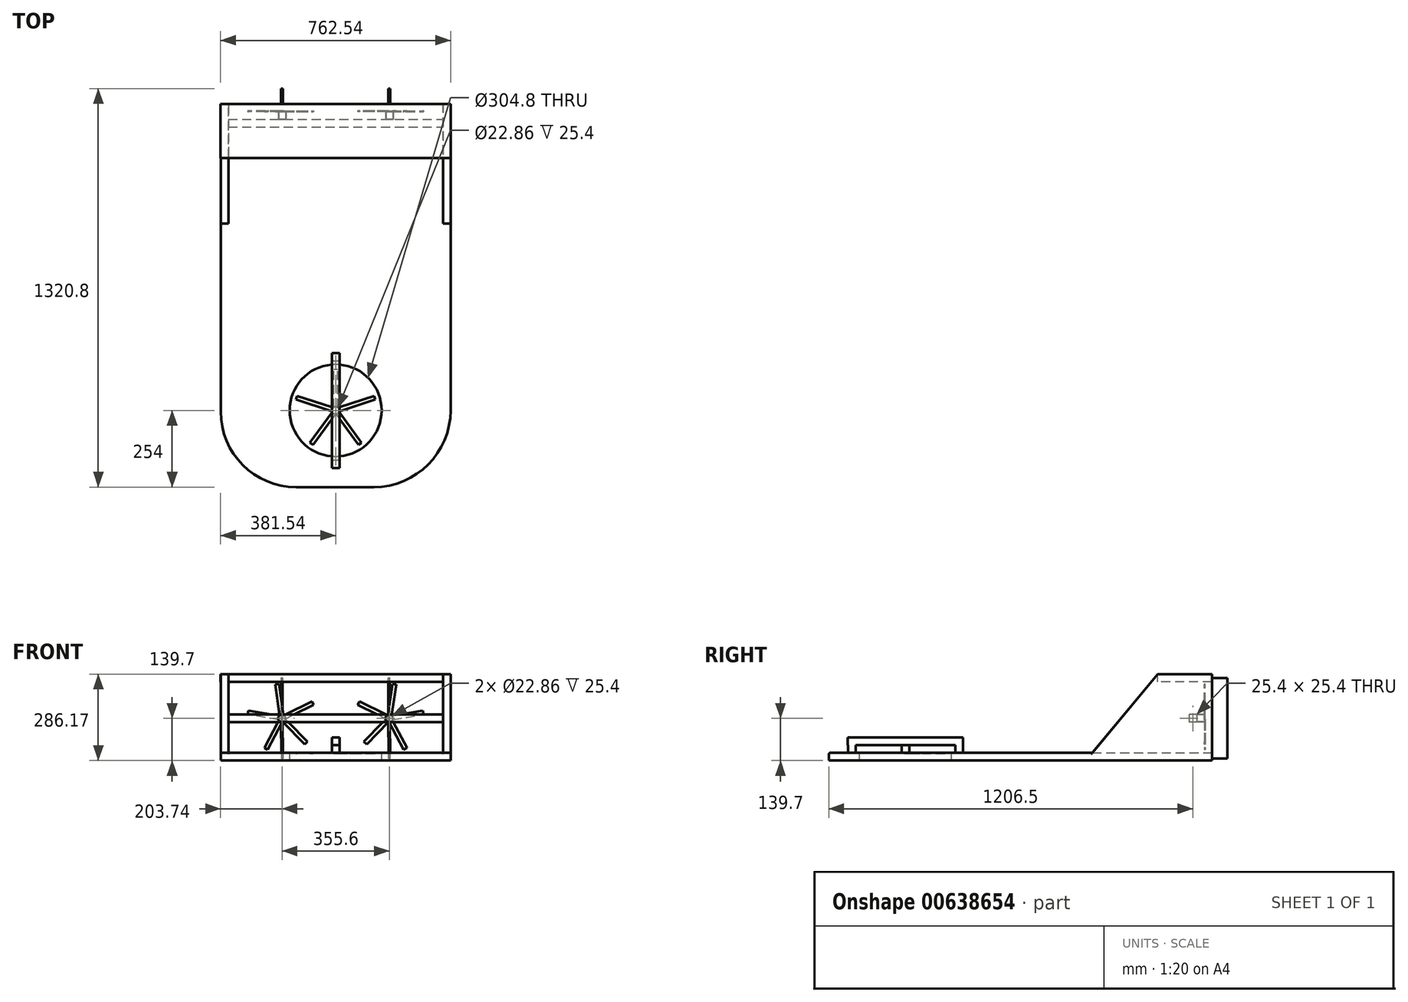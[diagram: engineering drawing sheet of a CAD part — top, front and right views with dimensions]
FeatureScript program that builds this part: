
annotation { "Feature Type Name" : "Feature", "Feature Type Description" : "" }
export const myFeature = defineFeature(function(context is Context, id is Id, definition is map)
    precondition{}
    {
        {
            var Q0;
            Q0=qCreatedBy(makeId("Top.planeOp"),FACE);
            var sketch = newSketch(context, id + "F0", { "sketchPlane" : qUnion([Q0])});
            skLineSegment(sketch, "E0.bottom", {"start": v(-381, 635) * mm, "end": v(381, 635) * mm});
            skLineSegment(sketch, "E0.top", {"start": v(-131, -635) * mm, "end": v(127, -635) * mm});
            skLineSegment(sketch, "E0.left", {"start": v(-381, 635) * mm, "end": v(-381, -385) * mm});
            skLineSegment(sketch, "E0.right", {"start": v(381, 635) * mm, "end": v(381, -381) * mm});
            skPoint(sketch, "E0.middle", {"position": v(0, 0) * mm});
            skPoint(sketch, "E1.visualSharp", {"position": v(-381, -635) * mm});
            skArc(sketch, "E1.filletArc", {"start": v(-381, -385) * mm, "mid": v(-307.78, -561.78) * mm, "end": v(-131, -635) * mm});
            skPoint(sketch, "E2.visualSharp", {"position": v(381, -635) * mm});
            skArc(sketch, "E2.filletArc", {"start": v(127, -635) * mm, "mid": v(306.6, -560.6) * mm, "end": v(381, -381) * mm});
            skPoint(sketch, "E3", {"position": v(0, -381) * mm});
            skCircle(sketch, "E4", {"center": v(0, -381) * mm, "radius": 152.4 * mm});
            skSolve(sketch);
        }
        {
            var Q0;
            Q0 = qSketchRegion(id + "F0", true);
            extrude(context, id + "F1", {"entities" : qUnion([Q0]), "oppositeDirection" : true, "depth" : 25.4 * mm, "offsetDistance" : 25.4 * mm});
        }
        {
            var Q0;
            Q0=makeQuery(id+"F1.opExtrude","CAP_EDGE",EDGE,{"disambiguationData":[OSD([sQuery(id+"F0.wireOp",EDGE,"E0.left")])],"isStart":true});
            var Q1;
            Q1=makeQuery(id+"F1.opExtrude","CAP_EDGE",EDGE,{"disambiguationData":[OSD([sQuery(id+"F0.wireOp",EDGE,"E1.filletArc")])],"isStart":true});
            var Q2;
            Q2=makeQuery(id+"F1.opExtrude","CAP_EDGE",EDGE,{"disambiguationData":[OSD([sQuery(id+"F0.wireOp",EDGE,"E0.top")])],"isStart":true});
            var Q3;
            Q3=makeQuery(id+"F1.opExtrude","CAP_EDGE",EDGE,{"disambiguationData":[OSD([sQuery(id+"F0.wireOp",EDGE,"E2.filletArc")])],"isStart":true});
            var Q4;
            Q4=makeQuery(id+"F1.opExtrude","CAP_EDGE",EDGE,{"disambiguationData":[OSD([sQuery(id+"F0.wireOp",EDGE,"E0.right")])],"isStart":true});
            var Q5;
            Q5=makeQuery(id+"F1.opExtrude","CAP_EDGE",EDGE,{"disambiguationData":[OSD([sQuery(id+"F0.wireOp",EDGE,"E0.bottom")])],"isStart":true});
            fillet(context, id + "F2", {"entities" : qUnion([Q0, Q1, Q2, Q3, Q4, Q5]), "radius" : 5.08 * mm, "tangentPropagation" : true, "allowEdgeOverflow" : false});
        }
        {
            var Q0;
            Q0=makeQuery(id+"F1.opExtrude","CAP_FACE",FACE,{"disambiguationData":[OSD([sQuery(id+"F0.wireOp",EDGE,"E0.bottom"),sQuery(id+"F0.wireOp",EDGE,"E0.top"),sQuery(id+"F0.wireOp",EDGE,"E0.left"),sQuery(id+"F0.wireOp",EDGE,"E0.right"),sQuery(id+"F0.wireOp",EDGE,"E1.filletArc"),sQuery(id+"F0.wireOp",EDGE,"E2.filletArc"),sQuery(id+"F0.wireOp",EDGE,"E4")])],"isStart":true});
            var sketch = newSketch(context, id + "F3", { "sketchPlane" : qUnion([Q0])});
            skLineSegment(sketch, "E5.bottom", {"start": v(-12.7, -215.9) * mm, "end": v(12.7, -215.9) * mm});
            skLineSegment(sketch, "E5.top", {"start": v(-12.7, -190.5) * mm, "end": v(12.7, -190.5) * mm});
            skLineSegment(sketch, "E5.left", {"start": v(-12.7, -215.9) * mm, "end": v(-12.7, -190.5) * mm});
            skLineSegment(sketch, "E5.right", {"start": v(12.7, -215.9) * mm, "end": v(12.7, -190.5) * mm});
            skPoint(sketch, "E5.middle", {"position": v(0, -203.2) * mm});
            skLineSegment(sketch, "E6.bottom", {"start": v(-12.7, -545.89) * mm, "end": v(12.7, -545.89) * mm});
            skLineSegment(sketch, "E6.top", {"start": v(-12.7, -571.71) * mm, "end": v(12.7, -571.71) * mm});
            skLineSegment(sketch, "E6.left", {"start": v(-12.7, -545.89) * mm, "end": v(-12.7, -571.71) * mm});
            skLineSegment(sketch, "E6.right", {"start": v(12.7, -545.89) * mm, "end": v(12.7, -571.71) * mm});
            skPoint(sketch, "E6.middle", {"position": v(0, -558.8) * mm});
            skSolve(sketch);
        }
        {
            var Q0;
            Q0 = qSketchRegion(id + "F3", true);
            extrude(context, id + "F4", {"entities" : qUnion([Q0]), "operationType" : NewBodyOperationType.ADD, "depth" : 25.4 * mm, "offsetDistance" : 25.4 * mm});
        }
        {
            var Q0;
            Q0=makeQuery(id+"F4.opExtrude","CAP_FACE",FACE,{"disambiguationData":[OSD([sQuery(id+"F3.wireOp",EDGE,"E5.bottom"),sQuery(id+"F3.wireOp",EDGE,"E5.top"),sQuery(id+"F3.wireOp",EDGE,"E5.left"),sQuery(id+"F3.wireOp",EDGE,"E5.right")])],"isStart":false});
            var sketch = newSketch(context, id + "F5", { "sketchPlane" : qUnion([Q0])});
            skLineSegment(sketch, "E7.bottom", {"start": v(-12.7, -190.5) * mm, "end": v(12.7, -190.5) * mm});
            skLineSegment(sketch, "E7.top", {"start": v(-12.7, -571.85) * mm, "end": v(12.7, -571.85) * mm});
            skLineSegment(sketch, "E7.left", {"start": v(-12.7, -190.5) * mm, "end": v(-12.7, -571.85) * mm});
            skLineSegment(sketch, "E7.right", {"start": v(12.7, -190.5) * mm, "end": v(12.7, -571.85) * mm});
            skSolve(sketch);
        }
        {
            var Q0;
            Q0 = qSketchRegion(id + "F5", true);
            extrude(context, id + "F6", {"entities" : qUnion([Q0]), "operationType" : NewBodyOperationType.ADD, "depth" : 25.4 * mm, "offsetDistance" : 25.4 * mm});
        }
        {
            var Q0;
            Q0=makeQuery(id+"F1.opExtrude","SWEPT_FACE",FACE,{"disambiguationData":[OSD([sQuery(id+"F0.wireOp",EDGE,"E0.right")])]});
            var sketch = newSketch(context, id + "F7", { "sketchPlane" : qUnion([Q0])});
            skLineSegment(sketch, "E8", {"start": v(635, -5.08) * mm, "end": v(635, 260.77) * mm});
            skLineSegment(sketch, "E9", {"start": v(635, 260.77) * mm, "end": v(455.73, 260.77) * mm});
            skLineSegment(sketch, "E10", {"start": v(455.73, 260.77) * mm, "end": v(234.4, -5.08) * mm});
            skLineSegment(sketch, "E11", {"start": v(234.4, -5.08) * mm, "end": v(635, -5.08) * mm});
            skSolve(sketch);
        }
        {
            var Q0;
            Q0 = qSketchRegion(id + "F7", true);
            extrude(context, id + "F8", {"entities" : qUnion([Q0]), "oppositeDirection" : true, "depth" : 25.4 * mm, "offsetDistance" : 25.4 * mm});
        }
        {
            var Q0;
            Q0=makeQuery(id+"F8.opExtrude","SWEPT_BODY",BODY,{"disambiguationData":[OSD([sQuery(id+"F7.wireOp",EDGE,"E8"),sQuery(id+"F7.wireOp",EDGE,"E9"),sQuery(id+"F7.wireOp",EDGE,"E10"),sQuery(id+"F7.wireOp",EDGE,"E11")])]});
            var Q1;
            Q1=qCreatedBy(makeId("Right.planeOp"),FACE);
            mirror(context, id + "F9", {"operationType" : NewBodyOperationType.ADD, "entities" : qUnion([Q0]), "mirrorPlane" : qUnion([Q1])});
        }
        {
            var Q0;
            Q0=makeQuery(id+"F8.opExtrude","SWEPT_FACE",FACE,{"disambiguationData":[OSD([sQuery(id+"F7.wireOp",EDGE,"E9")])]});
            var sketch = newSketch(context, id + "F10", { "sketchPlane" : qUnion([Q0])});
            skLineSegment(sketch, "E12.bottom", {"start": v(381, 635) * mm, "end": v(-381.54, 635) * mm});
            skLineSegment(sketch, "E12.top", {"start": v(381, 455.3) * mm, "end": v(-381.54, 455.3) * mm});
            skLineSegment(sketch, "E12.left", {"start": v(381, 635) * mm, "end": v(381, 455.3) * mm});
            skLineSegment(sketch, "E12.right", {"start": v(-381.54, 635) * mm, "end": v(-381.54, 455.3) * mm});
            skSolve(sketch);
        }
        {
            var Q0;
            {var subQ3=sQuery(id+"F10.wireOp",EDGE,"E12.top");Q0=makeQuery(id+"F10.imprint","IMPRINT",FACE,{"disambiguationData":[TD([[makeQuery(id+"F10.imprint","IMPRINT",EDGE,{"derivedFrom":subQ3}),-1.0]])]});}
            extrude(context, id + "F11", {"entities" : qUnion([Q0]), "operationType" : NewBodyOperationType.ADD, "oppositeDirection" : true, "depth" : 25.4 * mm, "offsetDistance" : 25.4 * mm});
        }
        {
            var Q0;
            Q0=makeQuery(id+"F8.opExtrude","CAP_FACE",FACE,{"disambiguationData":[OSD([sQuery(id+"F7.wireOp",EDGE,"E8"),sQuery(id+"F7.wireOp",EDGE,"E9"),sQuery(id+"F7.wireOp",EDGE,"E10"),sQuery(id+"F7.wireOp",EDGE,"E11")])],"isStart":false});
            var sketch = newSketch(context, id + "F12", { "sketchPlane" : qUnion([Q0])});
            skPoint(sketch, "E13", {"position": v(-571.5, 114.3) * mm});
            skLineSegment(sketch, "E14.bottom", {"start": v(-584.2, 127) * mm, "end": v(-558.8, 127) * mm});
            skLineSegment(sketch, "E14.top", {"start": v(-584.2, 101.6) * mm, "end": v(-558.8, 101.6) * mm});
            skLineSegment(sketch, "E14.left", {"start": v(-584.2, 127) * mm, "end": v(-584.2, 101.6) * mm});
            skLineSegment(sketch, "E14.right", {"start": v(-558.8, 127) * mm, "end": v(-558.8, 101.6) * mm});
            skSolve(sketch);
        }
        {
            var Q0;
            Q0 = qSketchRegion(id + "F12", true);
            extrude(context, id + "F13", {"entities" : qUnion([Q0]), "operationType" : NewBodyOperationType.ADD, "endBound" : BoundingType.UP_TO_NEXT, "depth" : 25.4 * mm, "offsetDistance" : 25.4 * mm});
        }
        {
            var Q0;
            Q0=makeQuery(id+"F13.opExtrude","SWEPT_FACE",FACE,{"disambiguationData":[OSD([sQuery(id+"F12.wireOp",EDGE,"E14.left")])]});
            var sketch = newSketch(context, id + "F14", { "sketchPlane" : qUnion([Q0])});
            skPoint(sketch, "E15", {"position": v(-177.8, 114.3) * mm});
            skPoint(sketch, "E16", {"position": v(177.8, 114.3) * mm});
            skPoint(sketch, "E17", {"position": v(-355.6, 114.3) * mm});
            skPoint(sketch, "E18", {"position": v(355.6, 114.3) * mm});
            skCircle(sketch, "E19", {"center": v(-177.8, 114.3) * mm, "radius": 12.7 * mm});
            skCircle(sketch, "E20", {"center": v(177.8, 114.3) * mm, "radius": 12.7 * mm});
            skCircle(sketch, "E21", {"center": v(-177.8, 114.3) * mm, "radius": 11.43 * mm});
            skCircle(sketch, "E22", {"center": v(177.8, 114.3) * mm, "radius": 11.43 * mm});
            skSolve(sketch);
        }
        {
            var Q0;
            Q0 = qSketchRegion(id + "F14", true);
            var Q1;
            Q1 = qConstructionFilter(qBodyType(qCreatedBy(id + "F14" ,EDGE), BodyType.WIRE), ConstructionObject.NO);
            extrude(context, id + "F15", {"entities" : qUnion([Q0]), "surfaceEntities" : qUnion([Q1]), "depth" : 25.4 * mm, "offsetDistance" : 25.4 * mm});
        }
        {
            var Q0;
            Q0=makeQuery(id+"F15.opExtrude","CAP_FACE",FACE,{"disambiguationData":[OSD([sQuery(id+"F14.wireOp",EDGE,"E19"),sQuery(id+"F14.wireOp",EDGE,"E21")])],"isStart":false});
            var sketch = newSketch(context, id + "F16", { "sketchPlane" : qUnion([Q0])});
            skPoint(sketch, "E23.0.midPoint", {"position": v(-135.12, 195.8) * mm});
            skLineSegment(sketch, "E24.0", {"start": v(-174.98, 108.61) * mm, "end": v(-73.09, 159.1) * mm});
            skLineSegment(sketch, "E25.0", {"start": v(-180.62, 119.99) * mm, "end": v(-78.73, 170.49) * mm});
            skLineSegment(sketch, "E26.0", {"start": v(-171.52, 115.22) * mm, "end": v(-188.06, 227.73) * mm});
            skLineSegment(sketch, "E27.0", {"start": v(-184.08, 113.38) * mm, "end": v(-200.62, 225.89) * mm});
            skLineSegment(sketch, "E28.0", {"start": v(-176.74, 120.56) * mm, "end": v(-288.85, 139.6) * mm});
            skLineSegment(sketch, "E29.0", {"start": v(-178.86, 108.04) * mm, "end": v(-290.98, 127.08) * mm});
            skLineSegment(sketch, "E30.0", {"start": v(-183.43, 117.25) * mm, "end": v(-236.18, 16.5) * mm});
            skLineSegment(sketch, "E31.0", {"start": v(-172.17, 111.35) * mm, "end": v(-224.92, 10.61) * mm});
            skLineSegment(sketch, "E32.0", {"start": v(-182.34, 109.86) * mm, "end": v(-102.83, 28.56) * mm});
            skLineSegment(sketch, "E33.0", {"start": v(-173.26, 118.74) * mm, "end": v(-93.75, 37.44) * mm});
            skLineSegment(sketch, "E34", {"start": v(-78.73, 170.49) * mm, "end": v(-73.09, 159.1) * mm});
            skLineSegment(sketch, "E35", {"start": v(-200.62, 225.89) * mm, "end": v(-188.06, 227.73) * mm});
            skLineSegment(sketch, "E36", {"start": v(-290.98, 127.08) * mm, "end": v(-288.85, 139.6) * mm});
            skLineSegment(sketch, "E37", {"start": v(-236.18, 16.5) * mm, "end": v(-224.92, 10.61) * mm});
            skLineSegment(sketch, "E38", {"start": v(-102.83, 28.56) * mm, "end": v(-93.75, 37.44) * mm});
            skLineSegment(sketch, "E39.MirrorCS", {"start": v(176.74, 120.56) * mm, "end": v(288.85, 139.6) * mm});
            skLineSegment(sketch, "E40.MirrorCS", {"start": v(178.86, 108.04) * mm, "end": v(290.98, 127.08) * mm});
            skLineSegment(sketch, "E41.MirrorCS", {"start": v(290.98, 127.08) * mm, "end": v(288.85, 139.6) * mm});
            skLineSegment(sketch, "E42.MirrorCS", {"start": v(183.43, 117.25) * mm, "end": v(236.18, 16.5) * mm});
            skLineSegment(sketch, "E43.MirrorCS", {"start": v(236.18, 16.5) * mm, "end": v(224.92, 10.61) * mm});
            skLineSegment(sketch, "E44.MirrorCS", {"start": v(172.17, 111.35) * mm, "end": v(224.92, 10.61) * mm});
            skLineSegment(sketch, "E45.MirrorCS", {"start": v(182.34, 109.86) * mm, "end": v(102.83, 28.56) * mm});
            skLineSegment(sketch, "E46.MirrorCS", {"start": v(173.26, 118.74) * mm, "end": v(93.75, 37.44) * mm});
            skLineSegment(sketch, "E47.MirrorCS", {"start": v(102.83, 28.56) * mm, "end": v(93.75, 37.44) * mm});
            skLineSegment(sketch, "E48.MirrorCS", {"start": v(174.98, 108.61) * mm, "end": v(73.09, 159.1) * mm});
            skLineSegment(sketch, "E49.MirrorCS", {"start": v(180.62, 119.99) * mm, "end": v(78.73, 170.49) * mm});
            skLineSegment(sketch, "E50.MirrorCS", {"start": v(78.73, 170.49) * mm, "end": v(73.09, 159.1) * mm});
            skLineSegment(sketch, "E51.MirrorCS", {"start": v(171.52, 115.22) * mm, "end": v(188.06, 227.73) * mm});
            skLineSegment(sketch, "E52.MirrorCS", {"start": v(184.08, 113.38) * mm, "end": v(200.62, 225.89) * mm});
            skLineSegment(sketch, "E53.MirrorCS", {"start": v(200.62, 225.89) * mm, "end": v(188.06, 227.73) * mm});
            skSolve(sketch);
        }
        {
            var Q0;
            Q0 = qSketchRegion(id + "F16", true);
            extrude(context, id + "F17", {"entities" : qUnion([Q0]), "depth" : 2.54 * mm, "offsetDistance" : 25.4 * mm});
        }
        {
            var Q0;
            {var subQ0=makeQuery(id+"F8.opExtrude","SWEPT_FACE",FACE,{"disambiguationData":[OSD([sQuery(id+"F7.wireOp",EDGE,"E8")])]});Q0=makeQuery(id+"F11.boolean.opBoolean","MERGE",FACE,{"derivedFrom":[makeQuery(id+"F9.boolean.opBoolean","MERGE",FACE,{"derivedFrom":[makeQuery(id+"F1.opExtrude","SWEPT_FACE",FACE,{"disambiguationData":[OSD([sQuery(id+"F0.wireOp",EDGE,"E0.bottom")])]}),subQ0,makeQuery(id+"F9.opPattern","COPY",FACE,{"derivedFrom":subQ0,"instanceName":"1"})]}),makeQuery(id+"F11.opExtrude","SWEPT_FACE",FACE,{"disambiguationData":[OSD([sQuery(id+"F10.wireOp",EDGE,"E12.bottom")])]})]});}
            var sketch = newSketch(context, id + "F18", { "sketchPlane" : qUnion([Q0])});
            skPoint(sketch, "E54", {"position": v(-177.26, 248.07) * mm});
            skPoint(sketch, "E55", {"position": v(-177.8, -18.63) * mm});
            skPoint(sketch, "E56", {"position": v(177.8, -18.63) * mm});
            skPoint(sketch, "E57", {"position": v(178.34, 248.07) * mm});
            skLineSegment(sketch, "E58.0", {"start": v(-175.26, -18.64) * mm, "end": v(-174.72, 248.06) * mm});
            skLineSegment(sketch, "E59.0", {"start": v(-180.34, -18.63) * mm, "end": v(-179.8, 248.07) * mm});
            skLineSegment(sketch, "E60", {"start": v(-179.8, 248.07) * mm, "end": v(-174.72, 248.06) * mm});
            skLineSegment(sketch, "E61", {"start": v(-180.34, -18.63) * mm, "end": v(-175.26, -18.64) * mm});
            skLineSegment(sketch, "E62.0", {"start": v(175.8, 248.07) * mm, "end": v(175.26, -18.63) * mm});
            skLineSegment(sketch, "E63.0", {"start": v(180.88, 248.06) * mm, "end": v(180.34, -18.64) * mm});
            skLineSegment(sketch, "E64", {"start": v(175.8, 248.07) * mm, "end": v(180.88, 248.06) * mm});
            skLineSegment(sketch, "E65", {"start": v(175.26, -18.63) * mm, "end": v(180.34, -18.64) * mm});
            skSolve(sketch);
        }
        {
            var Q0;
            Q0 = qSketchRegion(id + "F18", true);
            extrude(context, id + "F19", {"entities" : qUnion([Q0]), "operationType" : NewBodyOperationType.ADD, "depth" : 50.8 * mm, "offsetDistance" : 25.4 * mm});
        }
        {
            var Q0;
            {var subQ0=sQuery(id+"F5.wireOp",EDGE,"E7.right");var subQ1=sQuery(id+"F5.wireOp",EDGE,"E7.left");Q0=makeQuery(id+"F6.boolean.opBoolean","SPLIT",FACE,{"disambiguationData":[TD([makeQuery(id+"F4.opExtrude","SWEPT_FACE",FACE,{"disambiguationData":[OSD([sQuery(id+"F3.wireOp",EDGE,"E5.bottom")])]})])],"derivedFrom":makeQuery(id+"F6.opExtrude","CAP_FACE",FACE,{"disambiguationData":[OSD([sQuery(id+"F5.wireOp",EDGE,"E7.bottom"),sQuery(id+"F5.wireOp",EDGE,"E7.top"),subQ1,subQ0])],"isStart":true})});}
            var sketch = newSketch(context, id + "F20", { "sketchPlane" : qUnion([Q0])});
            skPoint(sketch, "E66", {"position": v(0, 381) * mm});
            skCircle(sketch, "E67", {"center": v(0, 381) * mm, "radius": 12.7 * mm});
            skCircle(sketch, "E68", {"center": v(0, 381) * mm, "radius": 11.43 * mm});
            skSolve(sketch);
        }
        {
            var Q0;
            Q0 = qSketchRegion(id + "F20", true);
            extrude(context, id + "F21", {"entities" : qUnion([Q0]), "operationType" : NewBodyOperationType.ADD, "depth" : 25.4 * mm, "offsetDistance" : 25.4 * mm});
        }
        {
            var Q0;
            Q0=makeQuery(id+"F21.opExtrude","CAP_FACE",FACE,{"disambiguationData":[OSD([sQuery(id+"F20.wireOp",EDGE,"E67"),sQuery(id+"F20.wireOp",EDGE,"E68")])],"isStart":false});
            var sketch = newSketch(context, id + "F22", { "sketchPlane" : qUnion([Q0])});
            skPoint(sketch, "E69.0.midPoint", {"position": v(0, 491.28) * mm});
            skLineSegment(sketch, "E70.0", {"start": v(1.96, 374.96) * mm, "end": v(-127.68, 332.84) * mm});
            skLineSegment(sketch, "E71.0", {"start": v(-1.96, 387.04) * mm, "end": v(-131.6, 344.91) * mm});
            skLineSegment(sketch, "E72.0", {"start": v(5.14, 384.73) * mm, "end": v(-74.99, 495.02) * mm});
            skLineSegment(sketch, "E73.0", {"start": v(-5.14, 377.27) * mm, "end": v(-85.26, 487.55) * mm});
            skLineSegment(sketch, "E74.0", {"start": v(5.14, 377.27) * mm, "end": v(85.26, 487.55) * mm});
            skLineSegment(sketch, "E75.0", {"start": v(-5.14, 384.73) * mm, "end": v(74.99, 495.02) * mm});
            skLineSegment(sketch, "E76.0", {"start": v(-1.96, 374.96) * mm, "end": v(127.68, 332.84) * mm});
            skLineSegment(sketch, "E77.0", {"start": v(1.96, 387.04) * mm, "end": v(131.6, 344.91) * mm});
            skLineSegment(sketch, "E78.0", {"start": v(-6.35, 381) * mm, "end": v(-6.35, 244.68) * mm});
            skLineSegment(sketch, "E79.0", {"start": v(6.35, 381) * mm, "end": v(6.35, 244.68) * mm});
            skLineSegment(sketch, "E80", {"start": v(-85.26, 487.55) * mm, "end": v(-74.99, 495.02) * mm});
            skLineSegment(sketch, "E81", {"start": v(-131.6, 344.91) * mm, "end": v(-127.68, 332.84) * mm});
            skLineSegment(sketch, "E82", {"start": v(-6.35, 244.68) * mm, "end": v(6.35, 244.68) * mm});
            skLineSegment(sketch, "E83", {"start": v(127.68, 332.84) * mm, "end": v(131.6, 344.91) * mm});
            skLineSegment(sketch, "E84", {"start": v(85.26, 487.55) * mm, "end": v(74.99, 495.02) * mm});
            skSolve(sketch);
        }
        {
            var Q0;
            Q0 = qSketchRegion(id + "F22", true);
            extrude(context, id + "F23", {"entities" : qUnion([Q0]), "depth" : 2.54 * mm, "offsetDistance" : 25.4 * mm});
        }
        {
            var Q0;
            {var subQ0=makeQuery(id+"F8.opExtrude","SWEPT_FACE",FACE,{"disambiguationData":[OSD([sQuery(id+"F7.wireOp",EDGE,"E8")])]});Q0=makeQuery(id+"F11.boolean.opBoolean","MERGE",FACE,{"derivedFrom":[makeQuery(id+"F9.boolean.opBoolean","MERGE",FACE,{"derivedFrom":[makeQuery(id+"F1.opExtrude","SWEPT_FACE",FACE,{"disambiguationData":[OSD([sQuery(id+"F0.wireOp",EDGE,"E0.bottom")])]}),subQ0,makeQuery(id+"F9.opPattern","COPY",FACE,{"derivedFrom":subQ0,"instanceName":"1"})]}),makeQuery(id+"F11.opExtrude","SWEPT_FACE",FACE,{"disambiguationData":[OSD([sQuery(id+"F10.wireOp",EDGE,"E12.bottom")])]})]});}
            var sketch = newSketch(context, id + "F24", { "sketchPlane" : qUnion([Q0])});
            skArc(sketch, "E85", {"start": v(-381, 12.7) * mm, "mid": v(-419.1, -25.55) * mm, "end": v(-380.7, -63.5) * mm});
            skLineSegment(sketch, "E86", {"start": v(-380.7, -63.5) * mm, "end": v(380.24, -63.5) * mm});
            skArc(sketch, "E87", {"start": v(380.24, -63.5) * mm, "mid": v(418.34, -25.78) * mm, "end": v(381, 12.7) * mm});
            skLineSegment(sketch, "E88", {"start": v(-381, 12.7) * mm, "end": v(-381, -25.4) * mm});
            skLineSegment(sketch, "E89", {"start": v(381, -25.4) * mm, "end": v(381, 12.7) * mm});
            skLineSegment(sketch, "E90", {"start": v(381, -25.4) * mm, "end": v(-381, -25.4) * mm});
            skSolve(sketch);
        }
        {
            var Q0;
            Q0=makeQuery(id+"F24.imprint","IMPRINT",FACE,{"disambiguationData":[TD([[makeQuery(id+"F24.imprint","IMPRINT",EDGE,{"derivedFrom":sQuery(id+"F24.wireOp",EDGE,"E85")}),1.0]])]});
            var Q1;
            Q1=sQuery(id+"F24.wireOp",EDGE,"E85");
            var Q2;
            Q2=sQuery(id+"F24.wireOp",EDGE,"E88");
            var Q3;
            Q3=sQuery(id+"F24.wireOp",EDGE,"E86");
            var Q4;
            Q4=sQuery(id+"F24.wireOp",EDGE,"E87");
            var Q5;
            Q5=sQuery(id+"F24.wireOp",EDGE,"E89");
            extrude(context, id + "F25", {"entities" : qUnion([Q0]), "bodyType" : ToolBodyType.SURFACE, "surfaceEntities" : qUnion([Q1, Q2, Q3, Q4, Q5]), "oppositeDirection" : true, "depth" : 1016 * mm, "offsetDistance" : 25.4 * mm, "hasSecondDirection" : true, "secondDirectionOppositeDirection" : false, "secondDirectionDepth" : 25.4 * mm});
        }
        {
            var Q0;
            Q0 = qSketchRegion(id + "F24", true);
            var Q1;
            Q1=makeQuery(id+"F25.opExtrude","CAP_EDGE",EDGE,{"disambiguationData":[OSD([sQuery(id+"F24.wireOp",EDGE,"E87")])],"isStart":false});
            var Q2;
            Q2=makeQuery(id+"F1.opExtrude","CAP_EDGE",EDGE,{"disambiguationData":[OSD([sQuery(id+"F0.wireOp",EDGE,"E1.filletArc")])],"isStart":false});
            sweep(context, id + "F26", {"bodyType" : ToolBodyType.SURFACE, "profiles" : qUnion([Q0]), "surfaceProfiles" : qUnion([Q1]), "path" : qUnion([Q2])});
        }
    });
